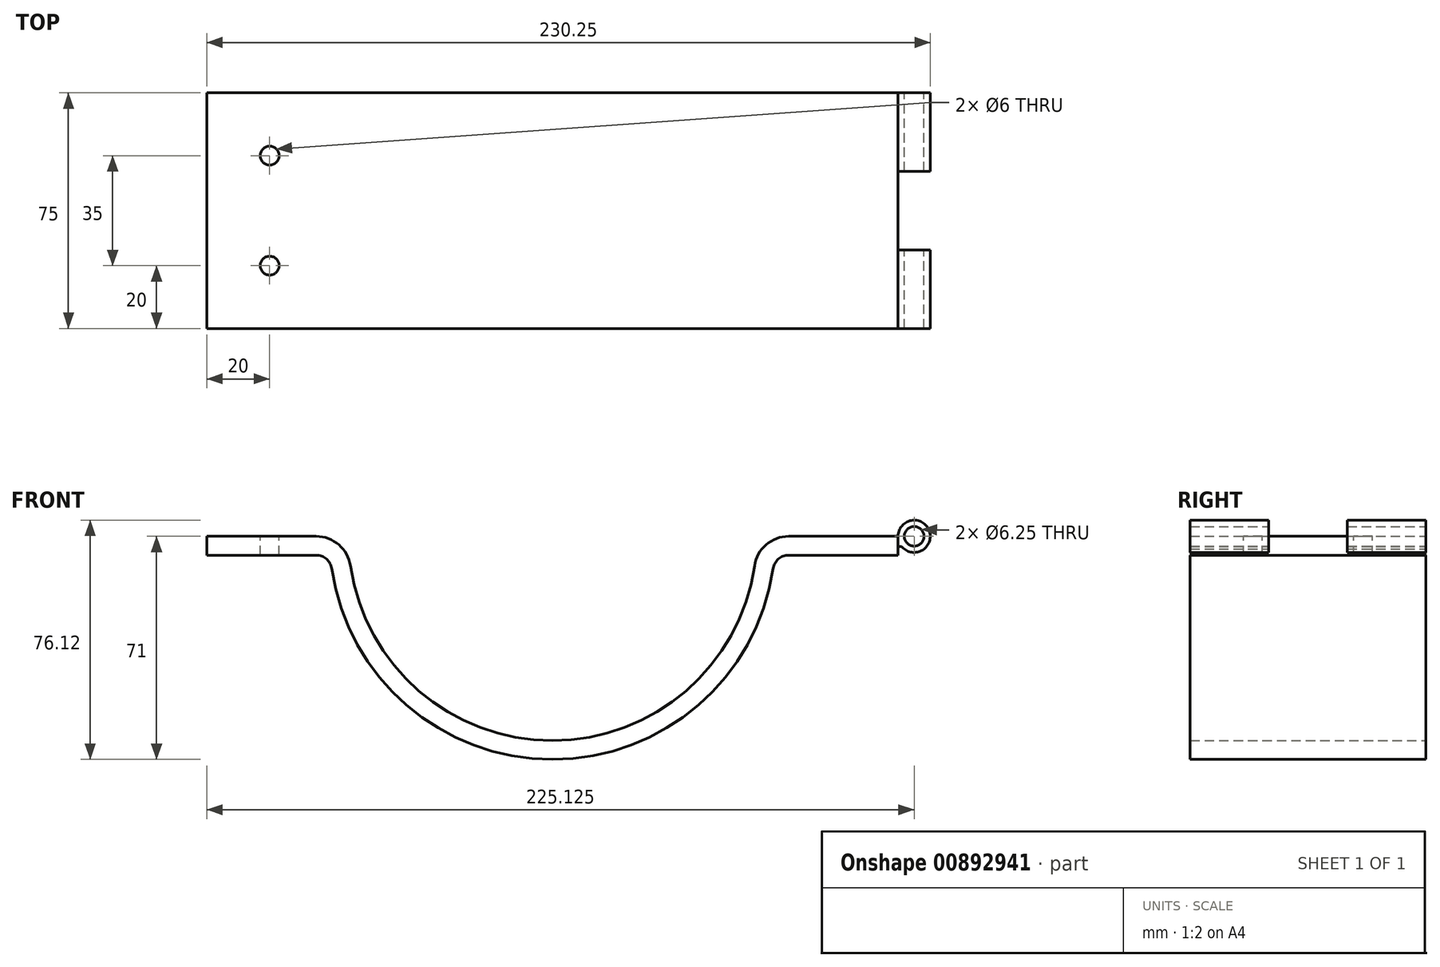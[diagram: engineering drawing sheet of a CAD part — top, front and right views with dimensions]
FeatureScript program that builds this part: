
annotation { "Feature Type Name" : "Feature", "Feature Type Description" : "" }
export const myFeature = defineFeature(function(context is Context, id is Id, definition is map)
    precondition{}
    {
        {
            var Q0;
            Q0=qCreatedBy(makeId("Front.planeOp"),FACE);
            var sketch = newSketch(context, id + "F0", { "sketchPlane" : qUnion([Q0])});
            skArc(sketch, "E0", {"start": v(-64.32, -9.4) * mm, "mid": v(0, -65) * mm, "end": v(64.32, -9.4) * mm});
            skArc(sketch, "E1", {"start": v(-70.25, -10.28) * mm, "mid": v(0, -71) * mm, "end": v(70.25, -10.28) * mm});
            skLineSegment(sketch, "E2", {"start": v(75.2, -6) * mm, "end": v(110, -6) * mm});
            skLineSegment(sketch, "E3", {"start": v(110, -6) * mm, "end": v(110, 0) * mm});
            skLineSegment(sketch, "E4.MirrorCS", {"start": v(-75.2, -6) * mm, "end": v(-110, -6) * mm});
            skLineSegment(sketch, "E5.MirrorCS", {"start": v(-110, -6) * mm, "end": v(-110, 0) * mm});
            skLineSegment(sketch, "E6", {"start": v(-110, 0) * mm, "end": v(-75.2, 0) * mm});
            skPoint(sketch, "E7.visualSharp", {"position": v(70.75, -6) * mm});
            skArc(sketch, "E7.filletArc", {"start": v(75.2, -6) * mm, "mid": v(71.93, -7.22) * mm, "end": v(70.25, -10.28) * mm});
            skPoint(sketch, "E8.newPointA", {"position": v(65, 0) * mm});
            skArc(sketch, "E8.filletArc", {"start": v(75.2, 0) * mm, "mid": v(68, -2.68) * mm, "end": v(64.32, -9.4) * mm});
            skLineSegment(sketch, "E9", {"start": v(75.2, 0) * mm, "end": v(110, 0) * mm});
            skPoint(sketch, "E10.visualSharp", {"position": v(-70.75, -6) * mm});
            skArc(sketch, "E10.filletArc", {"start": v(-70.25, -10.28) * mm, "mid": v(-71.93, -7.22) * mm, "end": v(-75.2, -6) * mm});
            skPoint(sketch, "E11.visualSharp", {"position": v(-65, 0) * mm});
            skArc(sketch, "E11.filletArc", {"start": v(-64.32, -9.4) * mm, "mid": v(-68, -2.68) * mm, "end": v(-75.2, 0) * mm});
            skSolve(sketch);
        }
        {
            var Q0;
            Q0=qSketchRegion(id+"F0",true);
            extrude(context, id + "F1", {"entities" : qUnion([Q0]), "endBound" : BoundingType.SYMMETRIC, "depth" : 75 * mm, "offsetDistance" : 25 * mm});
        }
        {
            var Q0;
            Q0=makeQuery(id+"F1.opExtrude","SWEPT_FACE",FACE,{"disambiguationData":[OSD([sQuery(id+"F0.wireOp",EDGE,"E6")])]});
            var sketch = newSketch(context, id + "F2", { "sketchPlane" : qUnion([Q0])});
            skLineSegment(sketch, "E12", {"start": v(-90, 40.03) * mm, "end": v(-90, -36.7) * mm, "construction": true});
            skLineSegment(sketch, "E13", {"start": v(-136.24, 0) * mm, "end": v(178.68, 0) * mm, "construction": true});
            skPoint(sketch, "E13.endSnap0", {"position": v(-75.2, 0) * mm});
            skLineSegment(sketch, "E14", {"start": v(0, -92.93) * mm, "end": v(0, 90.35) * mm, "construction": true});
            skCircle(sketch, "E15", {"center": v(-90, 17.5) * mm, "radius": 3 * mm});
            skCircle(sketch, "E16.MirrorC", {"center": v(-90, -17.5) * mm, "radius": 3 * mm});
            skSolve(sketch);
        }
        {
            var Q0;
            Q0=qCreatedBy(makeId("Front.planeOp"),FACE);
            var sketch = newSketch(context, id + "F3", { "sketchPlane" : qUnion([Q0])});
            skArc(sketch, "E17", {"start": v(111.34, -3.45) * mm, "mid": v(119.9, 1.85) * mm, "end": v(110, 0) * mm});
            skCircle(sketch, "E18", {"center": v(115.12, 0) * mm, "radius": 3.12 * mm});
            skArc(sketch, "E19", {"start": v(111.34, -3.45) * mm, "mid": v(110.5, -3.25) * mm, "end": v(110, -3.97) * mm});
            skLineSegment(sketch, "E20", {"start": v(110, -3.97) * mm, "end": v(110, 0) * mm});
            skSolve(sketch);
        }
        {
            var Q0;
            Q0 = qSketchRegion(id + "F3", true);
            var Q1;
            Q1=makeQuery(id+"F1.opExtrude","CAP_FACE",FACE,{"disambiguationData":[OSD([sQuery(id+"F0.wireOp",EDGE,"E0"),sQuery(id+"F0.wireOp",EDGE,"E1"),sQuery(id+"F0.wireOp",EDGE,"E2"),sQuery(id+"F0.wireOp",EDGE,"E3"),sQuery(id+"F0.wireOp",EDGE,"E4.MirrorCS"),sQuery(id+"F0.wireOp",EDGE,"E5.MirrorCS"),sQuery(id+"F0.wireOp",EDGE,"E6"),sQuery(id+"F0.wireOp",EDGE,"E7.filletArc"),sQuery(id+"F0.wireOp",EDGE,"E8.filletArc"),sQuery(id+"F0.wireOp",EDGE,"E9"),sQuery(id+"F0.wireOp",EDGE,"E10.filletArc"),sQuery(id+"F0.wireOp",EDGE,"E11.filletArc")])],"isStart":false});
            var Q2;
            Q2=makeQuery(id+"F1.opExtrude","CAP_FACE",FACE,{"disambiguationData":[OSD([sQuery(id+"F0.wireOp",EDGE,"E0"),sQuery(id+"F0.wireOp",EDGE,"E1"),sQuery(id+"F0.wireOp",EDGE,"E2"),sQuery(id+"F0.wireOp",EDGE,"E3"),sQuery(id+"F0.wireOp",EDGE,"E4.MirrorCS"),sQuery(id+"F0.wireOp",EDGE,"E5.MirrorCS"),sQuery(id+"F0.wireOp",EDGE,"E6"),sQuery(id+"F0.wireOp",EDGE,"E7.filletArc"),sQuery(id+"F0.wireOp",EDGE,"E8.filletArc"),sQuery(id+"F0.wireOp",EDGE,"E9"),sQuery(id+"F0.wireOp",EDGE,"E10.filletArc"),sQuery(id+"F0.wireOp",EDGE,"E11.filletArc")])],"isStart":true});
            extrude(context, id + "F4", {"entities" : qUnion([Q0]), "endBound" : BoundingType.UP_TO_SURFACE, "depth" : 25 * mm, "endBoundEntityFace" : qUnion([Q1]), "offsetDistance" : 25 * mm, "hasSecondDirection" : true, "secondDirectionBound" : SecondDirectionBoundingType.UP_TO_SURFACE, "secondDirectionOppositeDirection" : true, "secondDirectionDepth" : 25 * mm, "secondDirectionBoundEntityFace" : qUnion([Q2])});
        }
        {
            var Q0;
            Q0=qCreatedBy(makeId("Top.planeOp"),FACE);
            var sketch = newSketch(context, id + "F5", { "sketchPlane" : qUnion([Q0])});
            skLineSegment(sketch, "E21.bottom", {"start": v(110, -12.5) * mm, "end": v(122.73, -12.5) * mm});
            skLineSegment(sketch, "E21.top", {"start": v(110, 12.5) * mm, "end": v(122.73, 12.5) * mm});
            skLineSegment(sketch, "E21.left", {"start": v(110, -12.5) * mm, "end": v(110, 12.5) * mm});
            skLineSegment(sketch, "E21.right", {"start": v(122.73, -12.5) * mm, "end": v(122.73, 12.5) * mm});
            skSolve(sketch);
        }
        {
            var Q0;
            Q0 = qSketchRegion(id + "F5", true);
            extrude(context, id + "F6", {"entities" : qUnion([Q0]), "operationType" : NewBodyOperationType.REMOVE, "endBound" : BoundingType.THROUGH_ALL, "oppositeDirection" : true, "depth" : 25 * mm, "offsetDistance" : 25 * mm, "hasSecondDirection" : true, "secondDirectionBound" : SecondDirectionBoundingType.THROUGH_ALL, "secondDirectionOppositeDirection" : false, "secondDirectionDepth" : 25 * mm});
        }
        {
            var Q0;
            Q0 = qSketchRegion(id + "F2", true);
            extrude(context, id + "F7", {"entities" : qUnion([Q0]), "operationType" : NewBodyOperationType.REMOVE, "endBound" : BoundingType.THROUGH_ALL, "oppositeDirection" : true, "depth" : 25 * mm, "offsetDistance" : 25 * mm});
        }
    });
